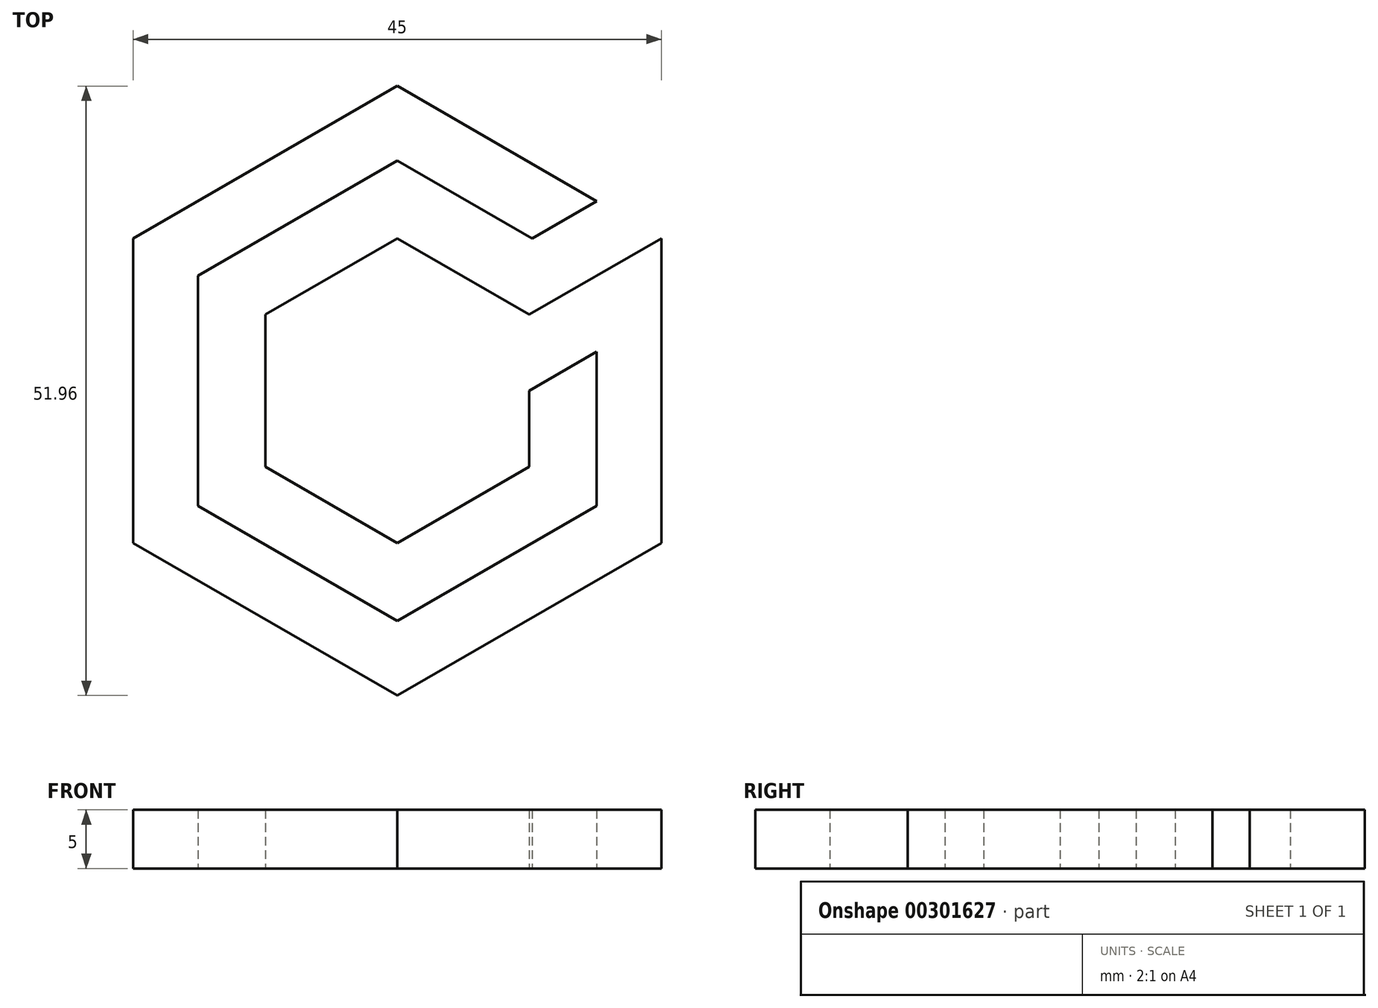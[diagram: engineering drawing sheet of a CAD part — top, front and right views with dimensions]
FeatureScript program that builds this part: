
annotation { "Feature Type Name" : "Feature", "Feature Type Description" : "" }
export const myFeature = defineFeature(function(context is Context, id is Id, definition is map)
    precondition{}
    {
        {
            var Q0;
            Q0=qCreatedBy(makeId("Top.planeOp"),FACE);
            var sketch = newSketch(context, id + "F0", { "sketchPlane" : qUnion([Q0])});
            skCircle(sketch, "E0.cCircle", {"center": v(0, 0) * mm, "radius": 22.5 * mm, "construction": true});
            skLineSegment(sketch, "E0.0", {"start": v(22.5, 13) * mm, "end": v(22.5, -13) * mm});
            skLineSegment(sketch, "E0.1", {"start": v(22.5, -13) * mm, "end": v(0, -25.98) * mm});
            skLineSegment(sketch, "E0.2", {"start": v(0, -25.98) * mm, "end": v(-22.5, -13) * mm});
            skLineSegment(sketch, "E0.3", {"start": v(-22.5, -13) * mm, "end": v(-22.5, 13) * mm});
            skLineSegment(sketch, "E0.4", {"start": v(-22.5, 13) * mm, "end": v(0, 25.98) * mm});
            skLineSegment(sketch, "E0.5", {"start": v(0, 25.98) * mm, "end": v(22.5, 13) * mm});
            skPoint(sketch, "E0.0.midPoint", {"position": v(22.5, 0) * mm});
            skCircle(sketch, "E1.cCircle", {"center": v(0, 0) * mm, "radius": 17 * mm, "construction": true});
            skLineSegment(sketch, "E1.0", {"start": v(17, 9.81) * mm, "end": v(17, -9.81) * mm});
            skLineSegment(sketch, "E1.1", {"start": v(17, -9.81) * mm, "end": v(0, -19.63) * mm});
            skLineSegment(sketch, "E1.2", {"start": v(0, -19.63) * mm, "end": v(-17, -9.81) * mm});
            skLineSegment(sketch, "E1.3", {"start": v(-17, -9.81) * mm, "end": v(-17, 9.81) * mm});
            skLineSegment(sketch, "E1.4", {"start": v(-17, 9.81) * mm, "end": v(0, 19.63) * mm});
            skLineSegment(sketch, "E1.5", {"start": v(0, 19.63) * mm, "end": v(17, 9.81) * mm});
            skPoint(sketch, "E1.0.midPoint", {"position": v(17, 0) * mm});
            skCircle(sketch, "E2.cCircle", {"center": v(0, 0) * mm, "radius": 11.25 * mm, "construction": true});
            skPoint(sketch, "E2.cCircle.perimeterSnap0", {"position": v(11.25, 19.49) * mm});
            skLineSegment(sketch, "E2.0", {"start": v(11.25, 6.5) * mm, "end": v(11.25, -6.5) * mm});
            skLineSegment(sketch, "E2.1", {"start": v(11.25, -6.5) * mm, "end": v(0, -13) * mm});
            skLineSegment(sketch, "E2.2", {"start": v(0, -13) * mm, "end": v(-11.25, -6.5) * mm});
            skLineSegment(sketch, "E2.3", {"start": v(-11.25, -6.5) * mm, "end": v(-11.25, 6.5) * mm});
            skLineSegment(sketch, "E2.4", {"start": v(-11.25, 6.5) * mm, "end": v(0, 13) * mm});
            skLineSegment(sketch, "E2.5", {"start": v(0, 13) * mm, "end": v(11.25, 6.5) * mm});
            skPoint(sketch, "E2.0.midPoint", {"position": v(11.25, 0) * mm});
            skPoint(sketch, "E2.0.midPoint.positionSnap0", {"position": v(11.25, 19.49) * mm});
            skLineSegment(sketch, "E3", {"start": v(-11.25, 6.5) * mm, "end": v(0, 0) * mm});
            skLineSegment(sketch, "E4", {"start": v(0, 0) * mm, "end": v(11.25, 6.5) * mm});
            skLineSegment(sketch, "E5", {"start": v(0, 0) * mm, "end": v(0, -13) * mm});
            skLineSegment(sketch, "E6", {"start": v(-17, 9.81) * mm, "end": v(-22.5, 13) * mm});
            skLineSegment(sketch, "E7", {"start": v(17, 9.81) * mm, "end": v(11.25, 6.5) * mm});
            skLineSegment(sketch, "E8", {"start": v(17, 16.17) * mm, "end": v(11.5, 13) * mm});
            skLineSegment(sketch, "E9", {"start": v(22.5, 13) * mm, "end": v(17, 9.81) * mm});
            skLineSegment(sketch, "E10", {"start": v(0, -19.63) * mm, "end": v(0, -25.98) * mm});
            skLineSegment(sketch, "E11", {"start": v(11.25, 0) * mm, "end": v(17, 3.32) * mm});
            skSolve(sketch);
        }
        {
            var Q0;
            Q0=makeQuery(id+"F0.imprint","IMPRINT",FACE,{"disambiguationData":[TD([[makeQuery(id+"F0.imprint","IMPRINT",EDGE,{"derivedFrom":sQuery(id+"F0.wireOp",EDGE,"E0.2")}),-1.0]])]});
            var Q1;
            {var subQ4=sQuery(id+"F0.wireOp",EDGE,"E0.4");Q1=makeQuery(id+"F0.imprint","IMPRINT",FACE,{"disambiguationData":[TD([[makeQuery(id+"F0.imprint","IMPRINT",EDGE,{"derivedFrom":subQ4}),-1.0]])]});}
            var Q2;
            Q2=makeQuery(id+"F0.imprint","IMPRINT",FACE,{"disambiguationData":[TD([[makeQuery(id+"F0.imprint","IMPRINT",EDGE,{"derivedFrom":sQuery(id+"F0.wireOp",EDGE,"E0.0")}),-1.0]])]});
            var Q3;
            Q3=makeQuery(id+"F0.imprint","IMPRINT",FACE,{"disambiguationData":[TD([[makeQuery(id+"F0.imprint","IMPRINT",EDGE,{"derivedFrom":sQuery(id+"F0.wireOp",EDGE,"E2.4")}),-1.0]])]});
            var Q4;
            Q4=makeQuery(id+"F0.imprint","IMPRINT",FACE,{"disambiguationData":[TD([[makeQuery(id+"F0.imprint","IMPRINT",EDGE,{"derivedFrom":sQuery(id+"F0.wireOp",EDGE,"E2.2")}),-1.0]])]});
            var Q5;
            {var subQ1=sQuery(id+"F0.wireOp",EDGE,"E2.1");Q5=makeQuery(id+"F0.imprint","IMPRINT",FACE,{"disambiguationData":[TD([[makeQuery(id+"F0.imprint","IMPRINT",EDGE,{"derivedFrom":subQ1}),-1.0]])]});}
            var Q6;
            {var subQ0=sQuery(id+"F0.wireOp",EDGE,"E7");Q6=makeQuery(id+"F0.imprint","IMPRINT",FACE,{"disambiguationData":[TD([[makeQuery(id+"F0.imprint","IMPRINT",EDGE,{"derivedFrom":subQ0}),1.0]])]});}
            extrude(context, id + "F1", {"entities" : qUnion([Q0, Q1, Q2, Q3, Q4, Q5, Q6]), "depth" : 5 * mm});
        }
    });
